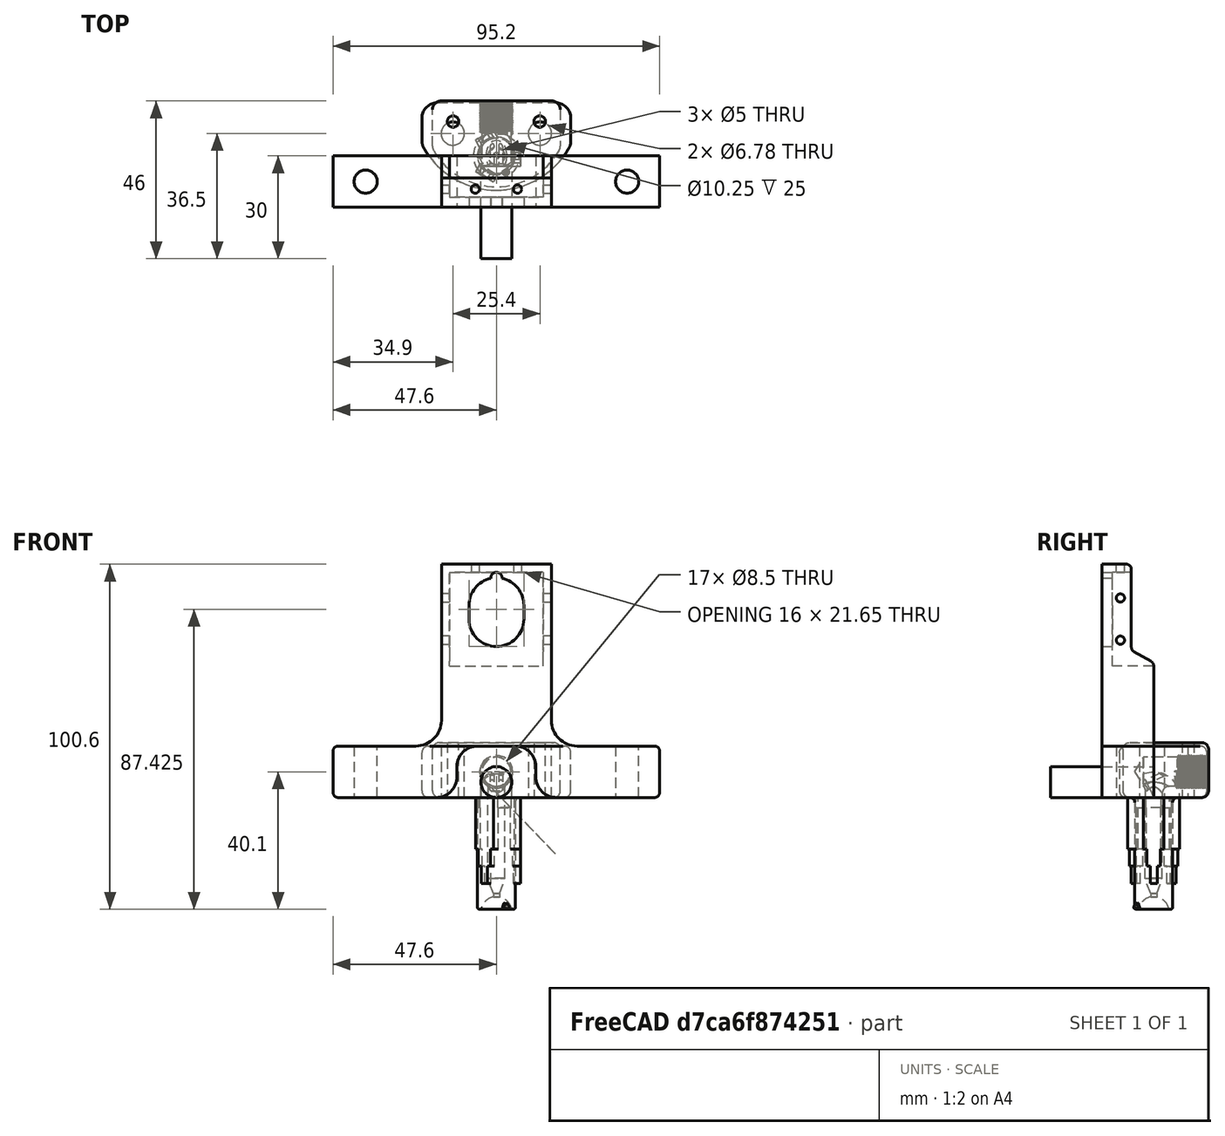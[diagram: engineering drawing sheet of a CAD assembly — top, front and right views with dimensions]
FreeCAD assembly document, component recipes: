
FREECAD ASSEMBLY — COMPONENT RECIPES ("Integrated-Inexpensive-Treadmill")

This assembly document has 6 components, labeled P0..P5 below (a component is one placed body or linked part). 6 of them carry a construction recipe — the FreeCAD feature program that regenerates the part from scratch, quoted from this document or its linked companion documents; the rest are supplied as boundary geometry only. No exploded tour is included for this assembly.
COMPONENT P0 — recipe-attached ("imperialBasePart", modeled in this document).
Construction recipe (the document's own serialized feature program — sketch geometry with constraints, then the solid features built on it; lengths are millimeters unless a unit is written):

FEATURE [Sketcher::SketchObject] Sketch005
  FullyConstrained = true
  MapMode = 5
  Support = -> [XY_Plane002]
  sketch-geometry (1):
    g0: Circle CenterX=0 CenterY=0 CenterZ=0 NormalX=0 NormalY=0 NormalZ=1 AngleXU=0 Radius=2.5
  constraints (2):
    c: Diameter(g0) = 5
    c: Coincident(g0,g-1)
FEATURE [Sketcher::SketchObject] Sketch007  label="imperialBaseSketch"
  FullyConstrained = true
  MapMode = 5
  Support = -> [XY_Plane002]
  sketch-geometry (16):
    g0: LineSegment StartX=-21.7 StartY=4.43042 StartZ=0 EndX=-21.7 EndY=11 EndZ=0
    g1: LineSegment StartX=-17.2 StartY=15.5 StartZ=0 EndX=17.2 EndY=15.5 EndZ=0
    g2: LineSegment StartX=21.7 StartY=11 StartZ=0 EndX=21.7 EndY=4.43042 EndZ=0
    g3: ArcOfCircle CenterX=1.7e-15 CenterY=14.3608 CenterZ=0 NormalX=0 NormalY=0 NormalZ=1 AngleXU=0 Radius=24.3608 StartAngle=3.66519 EndAngle=5.75959
    g4: ArcOfCircle CenterX=-17.2 CenterY=11 CenterZ=0 NormalX=0 NormalY=0 NormalZ=1 AngleXU=0 Radius=4.5 StartAngle=1.5708 EndAngle=3.14159
    g5: ArcOfCircle CenterX=17.2 CenterY=11 CenterZ=0 NormalX=0 NormalY=0 NormalZ=1 AngleXU=0 Radius=4.5 StartAngle=0 EndAngle=1.5708
    g6: ArcOfCircle CenterX=17.2 CenterY=4.43042 CenterZ=0 NormalX=0 NormalY=0 NormalZ=1 AngleXU=0 Radius=4.5 StartAngle=5.75959 EndAngle=6.28319
    g7: ArcOfCircle CenterX=-17.2 CenterY=4.43042 CenterZ=0 NormalX=0 NormalY=0 NormalZ=1 AngleXU=0 Radius=4.5 StartAngle=3.14159 EndAngle=3.66519
    g8: Circle CenterX=-12.7 CenterY=6.5 CenterZ=0 NormalX=0 NormalY=0 NormalZ=1 AngleXU=0 Radius=3.38865
    g9: Circle CenterX=12.7 CenterY=6.5 CenterZ=0 NormalX=0 NormalY=0 NormalZ=1 AngleXU=0 Radius=3.38865
    g10: GeomPoint X=-16.0886 Y=6.5 Z=0
    g11: GeomPoint X=16.0887 Y=6.5 Z=0
    g12: LineSegment StartX=-12.7 StartY=6.5 StartZ=0 EndX=12.7 EndY=6.5 EndZ=0
    g13: GeomPoint X=0 Y=-10 Z=0
    g14: GeomPoint X=0 Y=15.5 Z=0
    g15: GeomPoint X=0 Y=0 Z=0
  constraints (35):
    c: Vertical(g0)
    c: Vertical(g2)
    c: Tangent(g1,g4) = 1.5708
    c: Tangent(g0,g4) = 1.5708
    c: Tangent(g1,g5) = 1.5708
    c: Tangent(g2,g5) = 1.5708
    c: Tangent(g3,g6) = -1.5708
    c: Tangent(g2,g6) = 1.5708
    c: Tangent(g3,g7) = -1.5708
    c: Tangent(g0,g7) = 1.5708
    c: Diameter(g4) = 9
    c: Equal(g4,g7)
    c: Equal(g7,g5)
    c: Symmetric(g9,g8,g-2)
    c: Equal(g8,g9)
    c: Diameter(g9) = 6.7773
    c: PointOnObject(g10,g8)
    c: PointOnObject(g11,g9)
    c: Coincident(g12,g8)
    c: Coincident(g12,g9)
    c: PointOnObject(g11,g12)
    c: PointOnObject(g10,g12)
    c: DistanceX(g0,g8) = 9
    c: DistanceY(g8,g1) = 9
    c: Symmetric(g1,g1,g-2)
    c: PointOnObject(g13,g3)
    c: PointOnObject(g13,g-2)
    c: PointOnObject(g14,g1)
    c: PointOnObject(g14,g-2)
    c: Symmetric(g3,g3,g-2)
    c: Angle(g3) = 2.0944
    c: Coincident(g15,g-1)
    c: DistanceY(g15,g14) = 15.5
    c: DistanceY(g13,g15) = 10
    c: DistanceX(g8,g9) = 25.4
FEATURE [PartDesign::Pad] Pad001  label="imperialBase"
  AlongSketchNormal = false
  Direction = (0,0,1)
  Length = 15
  Length2 = 10
  Profile = -> Sketch007
  ReferenceAxis = -> Sketch007 [N_Axis]
  Type = 0
FEATURE [Sketcher::SketchObject] Sketch006
  FullyConstrained = true
  MapMode = 5
  Placement = pos=(0,15.5,0) rot=(0,0.707107,0.707107;3.14159rad)
  Support = -> [Pad001]
  sketch-geometry (1):
    g0: Circle CenterX=0 CenterY=7.5 CenterZ=0 NormalX=0 NormalY=0 NormalZ=1 AngleXU=0 Radius=4.7625
  constraints (3):
    c: PointOnObject(g0,g-2)
    c: DistanceY(g0,g-1) = -7.5
    c: Diameter(g0) = 9.525
FEATURE [PartDesign::Hole] Hole001  label="imperialThread"
  BaseFeature = -> Pad001
  CustomThreadClearance = 0
  Depth = 21
  DepthType = 0
  Diameter = 8.5
  DrillForDepth = true
  DrillPoint = 1
  DrillPointAngle = 118
  HoleCutCountersinkAngle = 90
  HoleCutCustomValues = false
  HoleCutDepth = 0
  HoleCutDiameter = 8.6
  HoleCutType = 0
  ModelThread = true
  Profile = -> Sketch006
  Tapered = false
  TaperedAngle = 90
  ThreadClass = 0
  ThreadDepth = 9
  ThreadDepthType = 1
  ThreadDirection = 0
  ThreadFit = 0
  ThreadSize = 12
  ThreadType = 4
  Threaded = true
  UseCustomThreadClearance = false
FEATURE [PartDesign::Pocket] Pocket001  label="imperialPocket"
  BaseFeature = -> Hole001
  Direction = (0,0,-1)
  Length = 6
  Length2 = 5
  Profile = -> Sketch005
  ReferenceAxis = -> Sketch005 [N_Axis]
  Reversed = true
  Type = 0
FEATURE [PartDesign::Fillet] Fillet004  label="outerEdgeFillet"
  Base = -> Pocket001 [Edge12,Edge14,Edge15,Edge11,Edge13,Edge6,Edge3,Edge9,Edge19,Edge10,Edge4,Edge7,Edge23,Edge22,Edge21,Edge20]
  BaseFeature = -> Pocket001
  Radius = 2
  SupportTransform = false
  UseAllEdges = false
FEATURE [PartDesign::Fillet] Fillet006
  Base = -> Fillet004 [Edge62]
  BaseFeature = -> Fillet004
  Radius = 2
  SupportTransform = false
  UseAllEdges = false
FEATURE [PartDesign::Body] Body002  label="imperialBaseBody"
  Group = -> [Sketch007,Pad001,Sketch006,Hole001,Sketch005,Pocket001,Fillet004,Fillet006]
  Origin = -> Origin002
  Tip = -> Fillet006
COMPONENT P1 — recipe-attached ("metricBasePart", modeled in this document).
Construction recipe (the document's own serialized feature program — sketch geometry with constraints, then the solid features built on it; lengths are millimeters unless a unit is written):

FEATURE [Sketcher::SketchObject] Sketch001  label="metricBaseSketch"
  FullyConstrained = true
  MapMode = 5
  Support = -> [XY_Plane001]
  sketch-geometry (16):
    g0: LineSegment StartX=-18.625 StartY=2.80977 StartZ=0 EndX=-18.625 EndY=13.5 EndZ=0
    g1: LineSegment StartX=-16.125 StartY=16 StartZ=0 EndX=16.125 EndY=16 EndZ=0
    g2: LineSegment StartX=18.625 StartY=13.5 StartZ=0 EndX=18.625 EndY=2.80977 EndZ=0
    g3: ArcOfCircle CenterX=1e-15 CenterY=12.1195 CenterZ=0 NormalX=0 NormalY=0 NormalZ=1 AngleXU=0 Radius=21.1195 StartAngle=3.66519 EndAngle=5.75959
    g4: ArcOfCircle CenterX=-16.125 CenterY=13.5 CenterZ=0 NormalX=0 NormalY=0 NormalZ=1 AngleXU=0 Radius=2.5 StartAngle=1.5708 EndAngle=3.14159
    g5: ArcOfCircle CenterX=16.125 CenterY=13.5 CenterZ=0 NormalX=0 NormalY=0 NormalZ=1 AngleXU=0 Radius=2.5 StartAngle=0 EndAngle=1.5708
    g6: ArcOfCircle CenterX=16.125 CenterY=2.80977 CenterZ=0 NormalX=0 NormalY=0 NormalZ=1 AngleXU=0 Radius=2.5 StartAngle=5.75959 EndAngle=6.28319
    g7: ArcOfCircle CenterX=-16.125 CenterY=2.80977 CenterZ=0 NormalX=0 NormalY=0 NormalZ=1 AngleXU=0 Radius=2.5 StartAngle=3.14159 EndAngle=3.66519
    g8: Circle CenterX=-12.625 CenterY=10 CenterZ=0 NormalX=0 NormalY=0 NormalZ=1 AngleXU=0 Radius=1.675
    g9: Circle CenterX=12.625 CenterY=10 CenterZ=0 NormalX=0 NormalY=0 NormalZ=1 AngleXU=0 Radius=1.675
    g10: GeomPoint X=-14.3 Y=10 Z=0
    g11: GeomPoint X=14.3 Y=10 Z=0
    g12: LineSegment StartX=-12.625 StartY=10 StartZ=0 EndX=12.625 EndY=10 EndZ=0
    g13: GeomPoint X=0 Y=-9 Z=0
    g14: GeomPoint X=0 Y=16 Z=0
    g15: GeomPoint X=0 Y=10 Z=0
  constraints (36):
    c: Vertical(g0)
    c: Vertical(g2)
    c: Tangent(g1,g4) = 1.5708
    c: Tangent(g0,g4) = 1.5708
    c: Tangent(g1,g5) = 1.5708
    c: Tangent(g2,g5) = 1.5708
    c: Tangent(g3,g6) = -1.5708
    c: Tangent(g2,g6) = 1.5708
    c: Tangent(g3,g7) = -1.5708
    c: Tangent(g0,g7) = 1.5708
    c: Diameter(g4) = 5
    c: Equal(g4,g7)
    c: Equal(g7,g5)
    c: Symmetric(g9,g8,g-2)
    c: Equal(g8,g9)
    c: Diameter(g9) = 3.35
    c: PointOnObject(g10,g8)
    c: PointOnObject(g11,g9)
    c: Coincident(g12,g8)
    c: Coincident(g12,g9)
    c: PointOnObject(g11,g12)
    c: PointOnObject(g10,g12)
    c: DistanceX(g10,g11) = 28.6
    c: DistanceX(g0,g8) = 6
    c: DistanceY(g8,g1) = 6
    c: Symmetric(g1,g1,g-2)
    c: PointOnObject(g13,g3)
    c: PointOnObject(g13,g-2)
    c: PointOnObject(g14,g1)
    c: PointOnObject(g14,g-2)
    c: Symmetric(g3,g3,g-2)
    c: Angle(g3) = 2.0944
    c: PointOnObject(g15,g12)
    c: PointOnObject(g15,g-2)
    c: DistanceY(g-1,g15) = 10
    c: DistanceY(g13,g-1) = 9
FEATURE [Sketcher::SketchObject] Sketch003
  FullyConstrained = true
  MapMode = 5
  Support = -> [XY_Plane001]
  sketch-geometry (1):
    g0: Circle CenterX=0 CenterY=0 CenterZ=0 NormalX=0 NormalY=0 NormalZ=1 AngleXU=0 Radius=2.5
  constraints (2):
    c: Diameter(g0) = 5
    c: Coincident(g0,g-1)
FEATURE [PartDesign::Pad] Pad  label="metricBase"
  Direction = (0,0,1)
  Length = 16
  Length2 = 10
  Profile = -> Sketch001
  ReferenceAxis = -> Sketch001 [N_Axis]
  Type = 0
FEATURE [Sketcher::SketchObject] Sketch002
  FullyConstrained = true
  MapMode = 5
  Placement = pos=(0,16,0) rot=(0,0.707107,0.707107;3.14159rad)
  Support = -> [Pad]
  sketch-geometry (1):
    g0: Circle CenterX=0 CenterY=7.5 CenterZ=0 NormalX=0 NormalY=0 NormalZ=1 AngleXU=0 Radius=4.7625
  constraints (3):
    c: PointOnObject(g0,g-2)
    c: DistanceY(g0,g-1) = -7.5
    c: Diameter(g0) = 9.525
FEATURE [PartDesign::Hole] Hole  label="metricThread"
  BaseFeature = -> Pad
  CustomThreadClearance = 0
  Depth = 19
  DepthType = 0
  Diameter = 8.5
  DrillForDepth = false
  DrillPoint = 0
  DrillPointAngle = 118
  HoleCutCountersinkAngle = 90
  HoleCutCustomValues = false
  HoleCutDepth = 0
  HoleCutDiameter = 8.6
  HoleCutType = 0
  ModelThread = true
  Profile = -> Sketch002
  Tapered = false
  TaperedAngle = 90
  ThreadClass = 0
  ThreadDepth = 9
  ThreadDepthType = 1
  ThreadDirection = 0
  ThreadFit = 0
  ThreadSize = 12
  ThreadType = 4
  Threaded = true
  UseCustomThreadClearance = false
FEATURE [PartDesign::Pocket] Pocket  label="metricAirOutlet"
  BaseFeature = -> Hole
  Direction = (0,0,-1)
  Length = 10
  Length2 = 5
  Profile = -> Sketch003
  ReferenceAxis = -> Sketch003 [N_Axis]
  Reversed = true
  Type = 0
FEATURE [PartDesign::Fillet] Fillet  label="BodyFillet"
  Base = -> Pocket [Edge12,Edge9,Edge3,Edge6,Edge11,Edge15,Edge13,Edge14,Edge19,Edge10,Edge4,Edge7,Edge23,Edge22,Edge21,Edge20]
  BaseFeature = -> Pocket
  Radius = 2
  SupportTransform = false
  UseAllEdges = false
FEATURE [PartDesign::Fillet] Fillet005  label="AirOutletFillet"
  Base = -> Fillet [Edge62]
  BaseFeature = -> Fillet
  Radius = 2
  SupportTransform = false
  UseAllEdges = false
FEATURE [PartDesign::Body] Body001  label="metricBaseBody"
  Group = -> [Sketch001,Pad,Sketch002,Hole,Sketch003,Pocket,Fillet,Fillet005]
  Origin = -> Origin001
  Tip = -> Fillet005
COMPONENT P2 — recipe-attached ("LightFixture", modeled in this document).
Construction recipe (the document's own serialized feature program — sketch geometry with constraints, then the solid features built on it; lengths are millimeters unless a unit is written):

FEATURE [Sketcher::SketchObject] Sketch017
  FullyConstrained = true
  MapMode = 5
  Support = -> [XY_Plane011]
  sketch-geometry (4):
    g0: LineSegment StartX=-4.5 StartY=3 StartZ=0 EndX=-4.5 EndY=0 EndZ=0
    g1: LineSegment StartX=-4.5 StartY=0 StartZ=0 EndX=4.5 EndY=0 EndZ=0
    g2: LineSegment StartX=4.5 StartY=0 StartZ=0 EndX=4.5 EndY=3 EndZ=0
    g3: ArcOfCircle CenterX=-3e-16 CenterY=3 CenterZ=0 NormalX=0 NormalY=0 NormalZ=1 AngleXU=0 Radius=4.5 StartAngle=0 EndAngle=3.14159
  constraints (12):
    c: PointOnObject(g0,g-1)
    c: Vertical(g0)
    c: Coincident(g0,g1)
    c: PointOnObject(g1,g-1)
    c: Coincident(g1,g2)
    c: Coincident(g3,g0)
    c: Coincident(g3,g2)
    c: Vertical(g2)
    c: Diameter(g3) = 9
    c: DistanceY(g0,g0) = 3
    c: Symmetric(g2,g0,g-2)
    c: Angle(g3) = 3.14159
FEATURE [PartDesign::Revolution] Revolution001  label="LightBody"
  Angle = 115
  Axis = (1,0,0)
  Base = (0,0,0)
  Profile = -> Sketch017
  ReferenceAxis = -> X_Axis011
FEATURE [Sketcher::SketchObject] Sketch018
  FullyConstrained = true
  MapMode = 5
  Placement = pos=(0,0,0) rot=(1,0,0;2.00713rad)
  Support = -> [Revolution001]
  sketch-geometry (2):
    g0: Circle CenterX=-1.27 CenterY=5 CenterZ=0 NormalX=0 NormalY=0 NormalZ=1 AngleXU=0 Radius=0.635
    g1: Circle CenterX=1.27 CenterY=5 CenterZ=0 NormalX=0 NormalY=0 NormalZ=1 AngleXU=0 Radius=0.635
  constraints (5):
    c: Symmetric(g1,g0,g-2)
    c: DistanceX(g0,g1) = 2.54
    c: Diameter(g1) = 1.27
    c: Equal(g0,g1)
    c: DistanceY(g-1,g1) = 5
FEATURE [PartDesign::Pocket] Pocket005  label="LED_Mounts"
  BaseFeature = -> Revolution001
  Direction = (0,0.906308,0.422618)
  Length = 5
  Length2 = 5
  Profile = -> Sketch018
  ReferenceAxis = -> Sketch018 [N_Axis]
  Type = 1
FEATURE [PartDesign::Body] Body005  label="Light"
  Group = -> [Sketch017,Revolution001,Sketch018,Pocket005]
  Origin = -> Origin011
  Tip = -> Pocket005
COMPONENT P3 — recipe-attached ("Connector", modeled in this document).
Construction recipe (the document's own serialized feature program — sketch geometry with constraints, then the solid features built on it; lengths are millimeters unless a unit is written):

FEATURE [Sketcher::SketchObject] Sketch019
  FullyConstrained = true
  MapMode = 5
  Placement = pos=(0,0,0) rot=(1,0,0;1.5708rad)
  Support = -> [XZ_Plane014]
  sketch-geometry (1):
    g0: Circle CenterX=0 CenterY=4.5 CenterZ=0 NormalX=0 NormalY=0 NormalZ=1 AngleXU=0 Radius=4.5
  constraints (3):
    c: PointOnObject(g0,g-2)
    c: Diameter(g0) = 9
    c: PointOnObject(g-1,g0)
FEATURE [PartDesign::Pad] Pad007  label="Rod"
  Direction = (0,-1,-2e-16)
  Length = 30
  Length2 = 10
  Placement = pos=(0,0,0) rot=(1,0,0;1.5708rad)
  Profile = -> Sketch019
  ReferenceAxis = -> Sketch019 [N_Axis]
  Type = 0
FEATURE [PartDesign::Body] Body006  label="ConnectorRod"
  Group = -> [Sketch019,Pad007]
  Origin = -> Origin013
  Tip = -> Pad007
COMPONENT P4 — recipe-attached ("FlirCameraHolder", modeled in this document).
Construction recipe (the document's own serialized feature program — sketch geometry with constraints, then the solid features built on it; lengths are millimeters unless a unit is written):

FEATURE [Sketcher::SketchObject] Sketch020
  FullyConstrained = true
  MapMode = 5
  Placement = pos=(0,0,0) rot=(1,0,0;1.5708rad)
  Support = -> [XZ_Plane016]
  expr: Constraints[20] = <<SphereHolderParameters>>.tubeheight + 20mm
  sketch-geometry (25):
    g0: LineSegment StartX=-47.6 StartY=1.5 StartZ=0 EndX=-47.6 EndY=13.5 EndZ=0
    g1: LineSegment StartX=-46.1 StartY=15 StartZ=0 EndX=-23.5 EndY=15 EndZ=0
    g2: LineSegment StartX=-16 StartY=22.5 StartZ=0 EndX=-16 EndY=68 EndZ=0
    g3: LineSegment StartX=-16 StartY=68 StartZ=0 EndX=16 EndY=68 EndZ=0
    g4: LineSegment StartX=16 StartY=68 StartZ=0 EndX=16 EndY=22.5 EndZ=0
    g5: LineSegment StartX=23.5 StartY=15 StartZ=0 EndX=46.1 EndY=15 EndZ=0
    g6: LineSegment StartX=47.6 StartY=13.5 StartZ=0 EndX=47.6 EndY=1.5 EndZ=0
    g7: LineSegment StartX=46.1 StartY=0 StartZ=0 EndX=17.5 EndY=0 EndZ=0
    g8: LineSegment StartX=-11.5 StartY=6 StartZ=0 EndX=-11.5 EndY=9 EndZ=0
    g9: LineSegment StartX=-5.5 StartY=15 StartZ=0 EndX=5.5 EndY=15 EndZ=0
    g10: LineSegment StartX=11.5 StartY=9 StartZ=0 EndX=11.5 EndY=6 EndZ=0
    g11: LineSegment StartX=-17.5 StartY=0 StartZ=0 EndX=-46.1 EndY=2e-16 EndZ=0
    g12: LineSegment StartX=-16 StartY=68 StartZ=0 EndX=16 EndY=36 EndZ=0
    g13: LineSegment StartX=16 StartY=68 StartZ=0 EndX=-16 EndY=36 EndZ=0
    g14: GeomPoint X=7e-15 Y=52 Z=0
    g15: ArcOfCircle CenterX=-17.5 CenterY=6 CenterZ=0 NormalX=0 NormalY=0 NormalZ=1 AngleXU=0 Radius=6 StartAngle=4.71239 EndAngle=6.28319
    g16: ArcOfCircle CenterX=-5.5 CenterY=9 CenterZ=0 NormalX=0 NormalY=0 NormalZ=1 AngleXU=0 Radius=6 StartAngle=1.5708 EndAngle=3.14159
    g17: ArcOfCircle CenterX=5.5 CenterY=9 CenterZ=0 NormalX=0 NormalY=0 NormalZ=1 AngleXU=0 Radius=6 StartAngle=0 EndAngle=1.5708
    g18: ArcOfCircle CenterX=17.5 CenterY=6 CenterZ=0 NormalX=0 NormalY=0 NormalZ=1 AngleXU=0 Radius=6 StartAngle=3.14159 EndAngle=4.71239
    g19: ArcOfCircle CenterX=23.5 CenterY=22.5 CenterZ=0 NormalX=0 NormalY=0 NormalZ=1 AngleXU=0 Radius=7.5 StartAngle=3.14159 EndAngle=4.71239
    g20: ArcOfCircle CenterX=-23.5 CenterY=22.5 CenterZ=0 NormalX=0 NormalY=0 NormalZ=1 AngleXU=0 Radius=7.5 StartAngle=4.71239 EndAngle=6.28319
    g21: ArcOfCircle CenterX=46.1 CenterY=13.5 CenterZ=0 NormalX=0 NormalY=0 NormalZ=1 AngleXU=0 Radius=1.5 StartAngle=3e-16 EndAngle=1.5708
    g22: ArcOfCircle CenterX=-46.1 CenterY=13.5 CenterZ=0 NormalX=0 NormalY=0 NormalZ=1 AngleXU=0 Radius=1.5 StartAngle=1.5708 EndAngle=3.14159
    g23: ArcOfCircle CenterX=46.1 CenterY=1.5 CenterZ=0 NormalX=0 NormalY=0 NormalZ=1 AngleXU=0 Radius=1.5 StartAngle=4.71239 EndAngle=6.28319
    g24: ArcOfCircle CenterX=-46.1 CenterY=1.5 CenterZ=0 NormalX=0 NormalY=0 NormalZ=1 AngleXU=0 Radius=1.5 StartAngle=3.14159 EndAngle=4.71239
  constraints (61):
    c: Vertical(g0)
    c: Horizontal(g1)
    c: Vertical(g2)
    c: Coincident(g2,g3)
    c: Horizontal(g3)
    c: Coincident(g3,g4)
    c: Vertical(g4)
    c: Horizontal(g5)
    c: Vertical(g6)
    c: Vertical(g8)
    c: Horizontal(g9)
    c: Vertical(g10)
    c: Coincident(g12,g2)
    c: PointOnObject(g12,g4)
    c: Coincident(g13,g3)
    c: PointOnObject(g13,g2)
    c: PointOnObject(g14,g13)
    c: PointOnObject(g14,g12)
    c: Angle(g13,g-2) = 0.785398
    c: Symmetric(g12,g13,g-2)
    c: DistanceY(g-1,g14) = 52
    c: Tangent(g11,g15) = 1.5708
    c: Tangent(g8,g15) = -1.5708
    c: Tangent(g8,g16) = 1.5708
    c: Tangent(g9,g16) = 1.5708
    c: Tangent(g9,g17) = 1.5708
    c: Tangent(g10,g17) = 1.5708
    c: Tangent(g10,g18) = -1.5708
    c: Tangent(g7,g18) = 1.5708
    c: Tangent(g4,g19) = -1.5708
    c: Tangent(g5,g19) = -1.5708
    c: Tangent(g2,g20) = -1.5708
    c: Tangent(g1,g20) = -1.5708
    c: Equal(g20,g19)
    c: Horizontal(g5,g1)
    c: DistanceX(g2,g3) = 32
    c: Tangent(g5,g21) = 1.5708
    c: Tangent(g6,g21) = 1.5708
    c: Tangent(g1,g22) = 1.5708
    c: Tangent(g0,g22) = 1.5708
    c: Tangent(g7,g23) = 1.5708
    c: Tangent(g6,g23) = 1.5708
    c: Tangent(g0,g24) = 1.5708
    c: Tangent(g11,g24) = 1.5708
    c: Equal(g22,g21)
    c: Equal(g21,g23)
    c: Equal(g23,g24)
    c: Diameter(g24) = 3
    c: PointOnObject(g11,g-1)
    c: Equal(g18,g17)
    c: Equal(g17,g16)
    c: Equal(g16,g15)
    c: Diameter(g15) = 12
    c: PointOnObject(g11,g-1)
    c: DistanceY(g-1,g5) = 15
    c: Symmetric(g8,g10,g-2)
    c: DistanceX(g8,g10) = 23
    c: DistanceY(g-1,g9) = 15
    c: Diameter(g20) = 15
    c: DistanceX(g0,g6) = 95.2
    c: Symmetric(g11,g7,g-2)
FEATURE [PartDesign::Pad] Pad008  label="OuterHull"
  Direction = (0,-1,2e-16)
  Length = 15
  Length2 = 10
  Placement = pos=(0,0,0) rot=(1,0,0;1.5708rad)
  Profile = -> Sketch020
  ReferenceAxis = -> Sketch020 [N_Axis]
  Type = 0
FEATURE [Sketcher::SketchObject] Sketch021
  ExternalGeometry = -> [Pad008]
  FullyConstrained = true
  MapMode = 5
  Placement = pos=(0,1e-16,0) rot=(-1,0,0;1.5708rad)
  Support = -> [Pad008]
  sketch-geometry (6):
    g0: LineSegment StartX=16 StartY=-68 StartZ=0 EndX=-52 EndY=0 EndZ=0
    g1: LineSegment StartX=-16 StartY=-68 StartZ=0 EndX=52 EndY=0 EndZ=0
    g2: LineSegment StartX=13.65 StartY=-65.65 StartZ=0 EndX=-13.65 EndY=-65.65 EndZ=0
    g3: LineSegment StartX=-13.65 StartY=-65.65 StartZ=0 EndX=-13.65 EndY=-38.35 EndZ=0
    g4: LineSegment StartX=-13.65 StartY=-38.35 StartZ=0 EndX=13.65 EndY=-38.35 EndZ=0
    g5: LineSegment StartX=13.65 StartY=-38.35 StartZ=0 EndX=13.65 EndY=-65.65 EndZ=0
  constraints (18):
    c: Coincident(g0,g-3)
    c: PointOnObject(g0,g-1)
    c: Coincident(g1,g-3)
    c: PointOnObject(g1,g-1)
    c: Angle(g1) = 0.785398
    c: Angle(g0) = 2.35619
    c: Coincident(g2,g3)
    c: Coincident(g3,g4)
    c: Coincident(g4,g5)
    c: Coincident(g5,g2)
    c: Horizontal(g2)
    c: Horizontal(g4)
    c: Vertical(g3)
    c: Vertical(g5)
    c: PointOnObject(g2,g0)
    c: PointOnObject(g3,g0)
    c: DistanceX(g3,g2) = 27.3
    c: PointOnObject(g2,g1)
FEATURE [PartDesign::Pocket] Pocket006  label="CameraCutout"
  BaseFeature = -> Pad008
  Direction = (0,-1,2e-16)
  Length = 12
  Length2 = 5
  Placement = pos=(0,0,0) rot=(1,0,0;1.5708rad)
  Profile = -> Sketch021
  ReferenceAxis = -> Sketch021 [N_Axis]
  Type = 0
FEATURE [Sketcher::SketchObject] Sketch022
  ExternalGeometry = -> [Pocket006]
  FullyConstrained = true
  MapMode = 5
  Placement = pos=(0,-12,2.6e-15) rot=(-1,0,0;1.5708rad)
  Support = -> [Pocket006]
  sketch-geometry (12):
    g0: LineSegment StartX=13.65 StartY=-65.65 StartZ=0 EndX=-52 EndY=0 EndZ=0
    g1: LineSegment StartX=-13.65 StartY=-65.65 StartZ=0 EndX=52 EndY=0 EndZ=0
    g2: GeomPoint X=0 Y=-52 Z=0
    g3: ArcOfCircle CenterX=0 CenterY=-56 CenterZ=0 NormalX=0 NormalY=0 NormalZ=1 AngleXU=0 Radius=8 StartAngle=3.14159 EndAngle=4.50577
    g4: ArcOfCircle CenterX=0 CenterY=-52 CenterZ=0 NormalX=0 NormalY=0 NormalZ=1 AngleXU=0 Radius=8 StartAngle=0 EndAngle=3.14159
    g5: LineSegment StartX=8 StartY=-56 StartZ=0 EndX=8 EndY=-52 EndZ=0
    g6: LineSegment StartX=-8 StartY=-52 StartZ=0 EndX=-8 EndY=-56 EndZ=0
    g7: GeomPoint X=0 Y=-64 Z=0
    g8: GeomPoint X=0 Y=-44 Z=0
    g9: ArcOfCircle CenterX=0 CenterY=-64 CenterZ=0 NormalX=0 NormalY=0 NormalZ=1 AngleXU=0 Radius=1.65 StartAngle=3.03828 EndAngle=6.38649
    g10: GeomPoint X=0 Y=-65.65 Z=0
    g11: ArcOfCircle CenterX=0 CenterY=-56 CenterZ=0 NormalX=0 NormalY=0 NormalZ=1 AngleXU=0 Radius=8 StartAngle=4.91901 EndAngle=6.28318
  constraints (30):
    c: Coincident(g0,g-3)
    c: PointOnObject(g0,g-1)
    c: Coincident(g1,g-3)
    c: PointOnObject(g1,g-1)
    c: Angle(g0) = 2.35619
    c: Angle(g1) = 0.785398
    c: PointOnObject(g2,g1)
    c: PointOnObject(g2,g-2)
    c: Coincident(g11,g5) = -1.5708
    c: Tangent(g5,g4) = -1.5708
    c: Tangent(g4,g6) = -1.5708
    c: Tangent(g6,g3) = -1.5708
    c: Equal(g3,g4)
    c: PointOnObject(g3,g-2)
    c: DistanceX(g4,g4) = 16
    c: PointOnObject(g7,g-2)
    c: PointOnObject(g8,g4)
    c: PointOnObject(g8,g-2)
    c: PointOnObject(g7,g3)
    c: DistanceY(g7,g8) = 20
    c: Coincident(g4,g2)
    c: Coincident(g9,g7)
    c: PointOnObject(g10,g9)
    c: PointOnObject(g10,g-2)
    c: PointOnObject(g10,g-3)
    c: Equal(g3,g11)
    c: Coincident(g3,g9)
    c: Coincident(g11,g9)
    c: Coincident(g3,g11)
    c: Vertical(g5)
FEATURE [PartDesign::Pocket] Pocket007  label="LensWindow"
  BaseFeature = -> Pocket006
  Direction = (0,-1,2e-16)
  Length = 5
  Length2 = 5
  Placement = pos=(0,0,0) rot=(1,0,0;1.5708rad)
  Profile = -> Sketch022
  ReferenceAxis = -> Sketch022 [N_Axis]
  Type = 0
FEATURE [Sketcher::SketchObject] Sketch023
  FullyConstrained = true
  MapMode = 5
  Placement = pos=(0,0,0) rot=(1,0,0;3.14159rad)
  Support = -> [Pocket007]
  sketch-geometry (2):
    g0: Circle CenterX=38.1 CenterY=7.5 CenterZ=0 NormalX=0 NormalY=0 NormalZ=1 AngleXU=0 Radius=3.3665
    g1: Circle CenterX=-38.1 CenterY=7.5 CenterZ=0 NormalX=0 NormalY=0 NormalZ=1 AngleXU=0 Radius=3.3665
  constraints (5):
    c: Equal(g1,g0)
    c: Diameter(g0) = 6.733
    c: DistanceY(g-1,g1) = 7.5
    c: Symmetric(g1,g0,g-2)
    c: DistanceX(g1,g0) = 76.2
FEATURE [PartDesign::Pocket] Pocket008  label="BottomScrews"
  BaseFeature = -> Pocket007
  Direction = (0,7e-16,1)
  Length = 5
  Length2 = 5
  Placement = pos=(0,0,0) rot=(1,0,0;1.5708rad)
  Profile = -> Sketch023
  ReferenceAxis = -> Sketch023 [N_Axis]
  Type = 1
FEATURE [Sketcher::SketchObject] Sketch024
  FullyConstrained = true
  MapMode = 5
  Placement = pos=(0,2.99e-14,68) rot=(0,0,1;3.14159rad)
  Support = -> [Pocket008]
  sketch-geometry (2):
    g0: Circle CenterX=-6.15 CenterY=9.7 CenterZ=0 NormalX=0 NormalY=0 NormalZ=1 AngleXU=0 Radius=1.2
    g1: Circle CenterX=6.15 CenterY=9.7 CenterZ=0 NormalX=0 NormalY=0 NormalZ=1 AngleXU=0 Radius=1.2
  constraints (5):
    c: Symmetric(g0,g1,g-2)
    c: Equal(g1,g0)
    c: Diameter(g0) = 2.4
    c: DistanceY(g-1,g0) = 9.7
    c: DistanceX(g0,g1) = 12.3
FEATURE [PartDesign::Pocket] Pocket009  label="TopScrews"
  BaseFeature = -> Pocket008
  Direction = (0,-8e-16,-1)
  Length = 5
  Length2 = 5
  Placement = pos=(0,0,0) rot=(1,0,0;1.5708rad)
  Profile = -> Sketch024
  ReferenceAxis = -> Sketch024 [N_Axis]
  Type = 2
FEATURE [Sketcher::SketchObject] Sketch026
  ExternalGeometry = -> [Pocket009]
  FullyConstrained = true
  MapMode = 5
  Placement = pos=(-13.65,0,0) rot=(0.707107,0,0.707107;3.14159rad)
  Support = -> [Pocket009]
  sketch-geometry (3):
    g0: Circle CenterX=45.85 CenterY=9.7 CenterZ=0 NormalX=0 NormalY=0 NormalZ=1 AngleXU=0 Radius=1.2
    g1: Circle CenterX=58.15 CenterY=9.7 CenterZ=0 NormalX=0 NormalY=0 NormalZ=1 AngleXU=0 Radius=1.2
    g2: LineSegment StartX=52 StartY=12 StartZ=0 EndX=52 EndY=0 EndZ=0
  constraints (8):
    c: PointOnObject(g2,g-5)
    c: PointOnObject(g2,g-1)
    c: Symmetric(g-5,g-5,g2)
    c: Symmetric(g1,g0,g2)
    c: DistanceX(g0,g1) = 12.3
    c: DistanceY(g1,g2) = 2.3
    c: Equal(g1,g0)
    c: Diameter(g0) = 2.4
FEATURE [PartDesign::Pocket] Pocket010  label="SideScrews"
  BaseFeature = -> Pocket009
  Direction = (-1,0,2e-16)
  Length = 5
  Length2 = 5
  Midplane = true
  Placement = pos=(0,0,0) rot=(1,0,0;1.5708rad)
  Profile = -> Sketch026
  ReferenceAxis = -> Sketch026 [N_Axis]
  Type = 1
FEATURE [Sketcher::SketchObject] Sketch027
  ExternalGeometry = -> [Pocket010]
  FullyConstrained = true
  MapMode = 5
  Placement = pos=(16,0,0) rot=(0.707107,0,0.707107;3.14159rad)
  Support = -> [Pocket010]
  sketch-geometry (7):
    g0: ArcOfCircle CenterX=66.5 CenterY=8 CenterZ=0 NormalX=0 NormalY=0 NormalZ=1 AngleXU=0 Radius=1.5 StartAngle=4.71239 EndAngle=6.28319
    g1: ArcOfCircle CenterX=38.35 CenterY=1.5 CenterZ=0 NormalX=0 NormalY=0 NormalZ=1 AngleXU=0 Radius=1.5 StartAngle=4.71239 EndAngle=5.75959
    g2: LineSegment StartX=43.8348 StartY=6.5 StartZ=0 EndX=66.5 EndY=6.5 EndZ=0
    g3: ArcOfCircle CenterX=43.8348 CenterY=5 CenterZ=0 NormalX=0 NormalY=0 NormalZ=1 AngleXU=0 Radius=1.5 StartAngle=1.5708 EndAngle=2.61799
    g4: LineSegment StartX=42.5358 StartY=5.75 StartZ=0 EndX=39.649 EndY=0.75 EndZ=0
    g5: LineSegment StartX=68 StartY=8 StartZ=0 EndX=68 EndY=0 EndZ=0
    g6: LineSegment StartX=68 StartY=0 StartZ=0 EndX=38.35 EndY=-8.4e-15 EndZ=0
  constraints (17):
    c: Coincident(g1,g-4)
    c: Perpendicular(g1,g-4)
    c: Diameter(g1) = 3
    c: Diameter(g0) = 3
    c: Tangent(g0,g-3) = -1.5708
    c: Horizontal(g2)
    c: Tangent(g4,g3) = -1.5708
    c: Diameter(g3) = 3
    c: Tangent(g3,g2) = 1.5708
    c: Tangent(g4,g1) = 1.5708
    c: Angle(g4) = -2.0944
    c: DistanceY(g-3,g0) = 6.5
    c: Tangent(g2,g0) = -1.5708
    c: Coincident(g5,g0)
    c: Coincident(g5,g-3)
    c: Coincident(g6,g5)
    c: Coincident(g6,g1)
FEATURE [PartDesign::Pocket] Pocket011  label="RaceLine"
  BaseFeature = -> Pocket010
  Direction = (-1,0,2e-16)
  Length = 5
  Length2 = 5
  Placement = pos=(0,0,0) rot=(1,0,0;1.5708rad)
  Profile = -> Sketch027
  ReferenceAxis = -> Sketch027 [N_Axis]
  Type = 1
FEATURE [PartDesign::Body] Body007  label="CameraBody"
  Group = -> [Sketch020,Pad008,Sketch021,Pocket006,Sketch022,Pocket007,Sketch023,Pocket008,Sketch024,Pocket009,Sketch026,Pocket010,Sketch027,Pocket011]
  Origin = -> Origin015
  Tip = -> Pocket011
COMPONENT P5 — recipe-attached ("TubePart", modeled in this document).
Construction recipe (the document's own serialized feature program — sketch geometry with constraints, then the solid features built on it; lengths are millimeters unless a unit is written):

FEATURE [Sketcher::SketchObject] Sketch  label="Revolution tube cross section"
  AttachmentOffset = pos=(0,0,0) rot=(1,0,0;3.14159rad)
  FullyConstrained = true
  MapMode = 5
  Placement = pos=(0,0,0) rot=(1,0,0;4.71239rad)
  Support = -> [XZ_Plane]
  expr: Constraints[12] = <<SphereHolderParameters>>.tubeheight
  sketch-geometry (10):
    g0: LineSegment StartX=-0.9 StartY=27.9713 StartZ=0 EndX=-0.9 EndY=28.9713 EndZ=0
    g1: LineSegment StartX=-2.5 StartY=8.9584e-12 StartZ=0 EndX=-6.73953 EndY=8.9584e-12 EndZ=0
    g2: LineSegment StartX=-5.5 StartY=1.47721 StartZ=0 EndX=-5.5 EndY=32 EndZ=0
    g3: ArcOfCircle CenterX=0 CenterY=33.3803 CenterZ=0 NormalX=0 NormalY=0 NormalZ=1 AngleXU=0 Radius=4.5 StartAngle=3.41593 EndAngle=4.51103
    g4: ArcOfCircle CenterX=0 CenterY=33.3803 CenterZ=0 NormalX=0 NormalY=0 NormalZ=1 AngleXU=0 Radius=4.5 StartAngle=3.41593 EndAngle=4.71239
    g5: ArcOfCircle CenterX=-4.90473 CenterY=32 CenterZ=0 NormalX=0 NormalY=0 NormalZ=1 AngleXU=0 Radius=0.595267 StartAngle=0.274335 EndAngle=3.14159
    g6: GeomPoint X=-5.5 Y=0 Z=0
    g7: ArcOfCircle CenterX=-7 CenterY=1.47721 CenterZ=0 NormalX=0 NormalY=0 NormalZ=1 AngleXU=0 Radius=1.5 StartAngle=4.88692 EndAngle=6.28319
    g8: LineSegment StartX=-0.9 StartY=27.9713 StartZ=0 EndX=-2.5 EndY=23.5753 EndZ=0
    g9: LineSegment StartX=-2.5 StartY=23.5753 StartZ=0 EndX=-2.5 EndY=8.9599e-12 EndZ=0
  constraints (29):
    c: Vertical(g0)
    c: PointOnObject(g6,g-1)
    c: Vertical(g2)
    c: PointOnObject(g3,g-2)
    c: Coincident(g3,g0)
    c: DistanceX(g6,g-1) = 5.5
    c: Coincident(g4,g3)
    c: PointOnObject(g4,g-2)
    c: Coincident(g3,g4)
    c: Tangent(g5,g3) = 1.5708
    c: Tangent(g5,g2) = 1.5708
    c: DistanceY(g0,g3) = 3.19
    c: DistanceY(g-1,g2) = 32
    c: PointOnObject(g6,g2)
    c: PointOnObject(g6,g1)
    c: Coincident(g7,g1)
    c: Tangent(g7,g2) = -1.5708
    c: Angle(g7) = 1.39626
    c: Diameter(g7) = 3
    c: Diameter(g3) = 9
    c: Coincident(g9,g8)
    c: Vertical(g9)
    c: Coincident(g0,g8)
    c: Coincident(g1,g9)
    c: DistanceX(g-2,g0) = -0.9
    c: Angle(g8) = 4.36332
    c: DistanceY(g0,g0) = 1
    c: Horizontal(g1)
    c: DistanceX(g1,g-1) = 2.5
FEATURE [PartDesign::Revolution] Revolution  label="Tube"
  Angle = 360
  Axis = (0,2e-16,-1)
  Base = (0,0,0)
  Placement = pos=(0,0,0) rot=(1,0,0;1.5708rad)
  Profile = -> Sketch
  ReferenceAxis = -> Sketch [V_Axis]
FEATURE [PartDesign::Plane] DatumPlane  label="Rotate120"
  AttachmentOffset = pos=(0,0,0) rot=(0,1,0;2.0944rad)
  Length = 79.989
  MapMode = 5
  Placement = pos=(0,0,0) rot=(-0.186157,0.694747,0.694747;3.50969rad)
  ResizeMode = 0
  Support = -> [YZ_Plane007]
  Width = 61.6877
FEATURE [PartDesign::Plane] DatumPlane001  label="Rotate240"
  AttachmentOffset = pos=(0,0,0) rot=(0,1,0;4.18879rad)
  Length = 79.989
  MapMode = 5
  Placement = pos=(0,0,0) rot=(-0.935113,0.250563,0.250563;4.64535rad)
  ResizeMode = 0
  Support = -> [YZ_Plane007]
  Width = 61.6877
FEATURE [Sketcher::SketchObject] Sketch008
  FullyConstrained = true
  MapMode = 5
  Placement = pos=(0,0,0) rot=(-0.186157,0.694747,0.694747;3.50969rad)
  Support = -> [DatumPlane]
  expr: Constraints[16] = Spreadsheet.tubeheight - 7mm
  expr: Constraints[17] = <<SphereHolderParameters>>.first_step
  expr: Constraints[32] = <<SphereHolderParameters>>.second_step
  sketch-geometry (12):
    g0: LineSegment StartX=-3 StartY=0 StartZ=0 EndX=3 EndY=-2e-16 EndZ=0
    g1: LineSegment StartX=2 StartY=-15 StartZ=0 EndX=2 EndY=-20 EndZ=0
    g2: LineSegment StartX=2 StartY=-20 StartZ=0 EndX=1 EndY=-20 EndZ=0
    g3: LineSegment StartX=1 StartY=-20 StartZ=0 EndX=1 EndY=-25 EndZ=0
    g4: LineSegment StartX=1 StartY=-25 StartZ=0 EndX=-1 EndY=-25 EndZ=0
    g5: LineSegment StartX=-1 StartY=-25 StartZ=0 EndX=-1 EndY=-20 EndZ=0
    g6: LineSegment StartX=-1 StartY=-20 StartZ=0 EndX=-2 EndY=-20 EndZ=0
    g7: LineSegment StartX=-2 StartY=-20 StartZ=0 EndX=-2 EndY=-15 EndZ=0
    g8: LineSegment StartX=-2 StartY=-15 StartZ=0 EndX=-3 EndY=-15 EndZ=0
    g9: LineSegment StartX=-3 StartY=-15 StartZ=0 EndX=-3 EndY=0 EndZ=0
    g10: LineSegment StartX=2 StartY=-15 StartZ=0 EndX=3 EndY=-15 EndZ=0
    g11: LineSegment StartX=3 StartY=-15 StartZ=0 EndX=3 EndY=0 EndZ=0
  constraints (33):
    c: PointOnObject(g0,g-1)
    c: Vertical(g1)
    c: Coincident(g1,g2)
    c: Horizontal(g2)
    c: Coincident(g2,g3)
    c: Vertical(g3)
    c: Coincident(g3,g4)
    c: Horizontal(g4)
    c: Coincident(g4,g5)
    c: Vertical(g5)
    c: Coincident(g5,g6)
    c: Horizontal(g6)
    c: Coincident(g6,g7)
    c: Vertical(g7)
    c: Symmetric(g0,g0,g-2)
    c: Symmetric(g5,g2,g-2)
    c: DistanceY(g3,g0) = 25
    c: DistanceY(g3,g2) = 5
    c: DistanceX(g4,g3) = 2
    c: DistanceX(g6,g1) = 4
    c: Horizontal(g8)
    c: Coincident(g9,g8)
    c: Vertical(g9)
    c: Coincident(g7,g8)
    c: Coincident(g0,g9)
    c: Horizontal(g10)
    c: Coincident(g11,g10)
    c: Vertical(g11)
    c: Coincident(g1,g10)
    c: Symmetric(g1,g7,g-2)
    c: Coincident(g0,g11)
    c: DistanceX(g8,g10) = 6
    c: DistanceY(g3,g10) = 10
FEATURE [PartDesign::Pad] Pad002
  Direction = (-0.5,0.866025,-5e-16)
  Length = 7
  Length2 = 10
  Placement = pos=(0,0,0) rot=(-0.186157,0.694747,0.694747;3.50969rad)
  Profile = -> Sketch008
  ReferenceAxis = -> Sketch008 [N_Axis]
  Type = 0
FEATURE [Sketcher::SketchObject] Sketch009
  FullyConstrained = true
  MapMode = 5
  Placement = pos=(0,0,0) rot=(0.935113,-0.250563,-0.250563;1.63783rad)
  Support = -> [DatumPlane001]
  expr: Constraints[27] = <<SphereHolderParameters>>.tubeheight - 7mm
  expr: Constraints[28] = <<SphereHolderParameters>>.first_step
  expr: Constraints[29] = <<SphereHolderParameters>>.second_step
  sketch-geometry (12):
    g0: LineSegment StartX=-3 StartY=0 StartZ=0 EndX=3 EndY=2e-16 EndZ=0
    g1: LineSegment StartX=3 StartY=2e-16 StartZ=0 EndX=3 EndY=-15 EndZ=0
    g2: LineSegment StartX=3 StartY=-15 StartZ=0 EndX=2 EndY=-15 EndZ=0
    g3: LineSegment StartX=2 StartY=-15 StartZ=0 EndX=2 EndY=-20 EndZ=0
    g4: LineSegment StartX=2 StartY=-20 StartZ=0 EndX=1 EndY=-20 EndZ=0
    g5: LineSegment StartX=1 StartY=-20 StartZ=0 EndX=1 EndY=-25 EndZ=0
    g6: LineSegment StartX=1 StartY=-25 StartZ=0 EndX=-1 EndY=-25 EndZ=0
    g7: LineSegment StartX=-1 StartY=-25 StartZ=0 EndX=-1 EndY=-20 EndZ=0
    g8: LineSegment StartX=-1 StartY=-20 StartZ=0 EndX=-2 EndY=-20 EndZ=0
    g9: LineSegment StartX=-2 StartY=-20 StartZ=0 EndX=-2 EndY=-15 EndZ=0
    g10: LineSegment StartX=-2 StartY=-15 StartZ=0 EndX=-3 EndY=-15 EndZ=0
    g11: LineSegment StartX=-3 StartY=-15 StartZ=0 EndX=-3 EndY=0 EndZ=0
  constraints (33):
    c: PointOnObject(g0,g-1)
    c: Coincident(g0,g1)
    c: Vertical(g1)
    c: Coincident(g1,g2)
    c: Horizontal(g2)
    c: Coincident(g2,g3)
    c: Vertical(g3)
    c: Coincident(g3,g4)
    c: Horizontal(g4)
    c: Coincident(g4,g5)
    c: Vertical(g5)
    c: Coincident(g5,g6)
    c: Horizontal(g6)
    c: Coincident(g6,g7)
    c: Vertical(g7)
    c: Coincident(g7,g8)
    c: Horizontal(g8)
    c: Coincident(g8,g9)
    c: Vertical(g9)
    c: Coincident(g9,g10)
    c: Horizontal(g10)
    c: Coincident(g10,g11)
    c: Coincident(g11,g0)
    c: Vertical(g11)
    c: Symmetric(g0,g0,g-2)
    c: Symmetric(g9,g2,g-2)
    c: Symmetric(g7,g4,g-2)
    c: DistanceY(g5,g0) = 25
    c: DistanceY(g6,g7) = 5
    c: DistanceY(g6,g9) = 10
    c: DistanceX(g0,g0) = 6
    c: DistanceX(g8,g3) = 4
    c: DistanceX(g6,g5) = 2
FEATURE [PartDesign::Pad] Pad003
  BaseFeature = -> Pad002
  Direction = (-0.5,-0.866025,3e-16)
  Length = 7
  Length2 = 10
  Placement = pos=(0,0,0) rot=(-0.186157,0.694747,0.694747;3.50969rad)
  Profile = -> Sketch009
  ReferenceAxis = -> Sketch009 [N_Axis]
  Type = 0
FEATURE [Sketcher::SketchObject] Sketch010
  FullyConstrained = true
  MapMode = 5
  Placement = pos=(0,0,0) rot=(0.57735,0.57735,0.57735;2.0944rad)
  Support = -> [YZ_Plane007]
  expr: Constraints[29] = <<SphereHolderParameters>>.tubeheight - 7mm
  expr: Constraints[30] = <<SphereHolderParameters>>.first_step
  expr: Constraints[31] = <<SphereHolderParameters>>.second_step
  sketch-geometry (12):
    g0: LineSegment StartX=-3 StartY=0 StartZ=0 EndX=3 EndY=0 EndZ=0
    g1: LineSegment StartX=3 StartY=0 StartZ=0 EndX=3 EndY=-15 EndZ=0
    g2: LineSegment StartX=3 StartY=-15 StartZ=0 EndX=2 EndY=-15 EndZ=0
    g3: LineSegment StartX=2 StartY=-15 StartZ=0 EndX=2 EndY=-20 EndZ=0
    g4: LineSegment StartX=2 StartY=-20 StartZ=0 EndX=1 EndY=-20 EndZ=0
    g5: LineSegment StartX=1 StartY=-20 StartZ=0 EndX=1 EndY=-25 EndZ=0
    g6: LineSegment StartX=1 StartY=-25 StartZ=0 EndX=-1 EndY=-25 EndZ=0
    g7: LineSegment StartX=-1 StartY=-25 StartZ=0 EndX=-1 EndY=-20 EndZ=0
    g8: LineSegment StartX=-1 StartY=-20 StartZ=0 EndX=-2 EndY=-20 EndZ=0
    g9: LineSegment StartX=-2 StartY=-20 StartZ=0 EndX=-2 EndY=-15 EndZ=0
    g10: LineSegment StartX=-2 StartY=-15 StartZ=0 EndX=-3 EndY=-15 EndZ=0
    g11: LineSegment StartX=-3 StartY=-15 StartZ=0 EndX=-3 EndY=0 EndZ=0
  constraints (32):
    c: PointOnObject(g0,g-1)
    c: PointOnObject(g0,g-1)
    c: Coincident(g0,g1)
    c: Vertical(g1)
    c: Coincident(g1,g2)
    c: Horizontal(g2)
    c: Coincident(g2,g3)
    c: Vertical(g3)
    c: Coincident(g3,g4)
    c: Horizontal(g4)
    c: Coincident(g4,g5)
    c: Vertical(g5)
    c: Coincident(g5,g6)
    c: Coincident(g6,g7)
    c: Coincident(g7,g8)
    c: Horizontal(g8)
    c: Coincident(g8,g9)
    c: Coincident(g9,g10)
    c: Coincident(g10,g11)
    c: Coincident(g11,g0)
    c: Vertical(g11)
    c: Vertical(g9)
    c: Symmetric(g6,g5,g-2)
    c: Symmetric(g4,g7,g-2)
    c: Symmetric(g2,g9,g-2)
    c: Symmetric(g1,g10,g-2)
    c: DistanceX(g6,g5) = 2
    c: DistanceX(g8,g3) = 4
    c: DistanceX(g10,g1) = 6
    c: DistanceY(g5,g0) = 25
    c: DistanceY(g5,g4) = 5
    c: DistanceY(g5,g2) = 10
FEATURE [PartDesign::Pad] Pad004
  BaseFeature = -> Pad003
  Direction = (1,-2e-16,3e-16)
  Length = 7
  Length2 = 10
  Placement = pos=(0,0,0) rot=(-0.186157,0.694747,0.694747;3.50969rad)
  Profile = -> Sketch010
  ReferenceAxis = -> Sketch010 [N_Axis]
  Type = 0
FEATURE [Sketcher::SketchObject] Sketch011
  FullyConstrained = true
  MapMode = 5
  Support = -> [XY_Plane007]
  sketch-geometry (1):
    g0: Circle CenterX=0 CenterY=0 CenterZ=0 NormalX=0 NormalY=0 NormalZ=1 AngleXU=0 Radius=5.25
  constraints (2):
    c: Coincident(g0,g-1)
    c: Diameter(g0) = 10.5
FEATURE [PartDesign::Pad] Pad005
  BaseFeature = -> Pad004
  Direction = (0,0,1)
  Length = 3
  Length2 = 10
  Placement = pos=(0,0,0) rot=(-0.186157,0.694747,0.694747;3.50969rad)
  Profile = -> Sketch011
  ReferenceAxis = -> Sketch011 [N_Axis]
  Reversed = true
  Type = 0
FEATURE [Sketcher::SketchObject] Sketch012
  FullyConstrained = true
  MapMode = 5
  Support = -> [XY_Plane007]
  sketch-geometry (1):
    g0: Circle CenterX=0 CenterY=0 CenterZ=0 NormalX=0 NormalY=0 NormalZ=1 AngleXU=0 Radius=5.125
  constraints (2):
    c: Coincident(g0,g-1)
    c: Diameter(g0) = 10.25
FEATURE [PartDesign::Pocket] Pocket002
  BaseFeature = -> Pad005
  Direction = (0,0,-1)
  Length = 5
  Length2 = 5
  Placement = pos=(0,0,0) rot=(-0.186157,0.694747,0.694747;3.50969rad)
  Profile = -> Sketch012
  ReferenceAxis = -> Sketch012 [N_Axis]
  Type = 1
FEATURE [PartDesign::Body] Body003  label="Steppers"
  Group = -> [DatumPlane,DatumPlane001,Sketch008,Pad002,Sketch009,Pad003,Sketch010,Pad004,Sketch011,Pad005,Sketch012,Pocket002]
  Origin = -> Origin007
  Tip = -> Pocket002
FEATURE [PartDesign::Plane] DatumPlane003
  Length = 60
  MapMode = 11
  Placement = pos=(0,0,-32) rot=(0.707107,0.707107,0;3.14159rad)
  ResizeMode = 0
  Support = -> [Revolution]
  Width = 60
FEATURE [Sketcher::SketchObject] Sketch030
  ExternalGeometry = -> [Revolution]
  FullyConstrained = true
  MapMode = 5
  Placement = pos=(0,0,-32) rot=(0.707107,0.707107,0;3.14159rad)
  Support = -> [DatumPlane003]
  sketch-geometry (3):
    g0: LineSegment StartX=0 StartY=0 StartZ=0 EndX=5.19615 EndY=3 EndZ=0
    g1: ArcOfCircle CenterX=4.76314 CenterY=2.75 CenterZ=0 NormalX=0 NormalY=0 NormalZ=1 AngleXU=0 Radius=1 StartAngle=5.14495 EndAngle=8.46862
    g2: ArcOfCircle CenterX=0 CenterY=0 CenterZ=0 NormalX=0 NormalY=0 NormalZ=1 AngleXU=0 Radius=5.5 StartAngle=0.341529 EndAngle=0.705668
  constraints (10):
    c: Coincident(g0,g-4)
    c: Distance(g0) = 6
    c: Angle(g0) = 0.523599
    c: PointOnObject(g1,g-3)
    c: PointOnObject(g1,g-3)
    c: Diameter(g1) = 2
    c: Coincident(g2,g0)
    c: Coincident(g2,g1)
    c: Coincident(g2,g1)
    c: PointOnObject(g1,g0)
FEATURE [PartDesign::Line] DatumLine001
  AttacherType = Attacher::AttachEngineLine
  Length = 20
  MapMode = 31
  Placement = pos=(2.70455,4.68441,-32) rot=(-0.377964,0.654654,0.654654;3.86433rad)
  ResizeMode = 0
  Support = -> [Sketch030]
FEATURE [PartDesign::Revolution] Revolution004  label="SensorHolderUnderpinning"
  Angle = 100
  Axis = (-0.866025,0.5,0)
  Base = (2.70455,4.68441,-32)
  BaseFeature = -> Revolution
  Placement = pos=(0,0,0) rot=(1,0,0;1.5708rad)
  Profile = -> Sketch030
  ReferenceAxis = -> DatumLine001
  Reversed = true
FEATURE [PartDesign::Revolution] Revolution005  label="SensorHolderAngle"
  Angle = 20
  Axis = (-0.866025,0.5,0)
  Base = (2.70455,4.68441,-32)
  BaseFeature = -> Revolution004
  Placement = pos=(0,0,0) rot=(1,0,0;1.5708rad)
  Profile = -> Sketch030
  ReferenceAxis = -> DatumLine001
FEATURE [Sketcher::SketchObject] Sketch031
  ExternalGeometry = -> [DatumLine001]
  FullyConstrained = true
  MapMode = 5
  Placement = pos=(-4.82593,-8.35875,-26.5183) rot=(0.996224,-0.013204,-0.085814;2.83738rad)
  Support = -> [Revolution005]
  sketch-geometry (2):
    g0: Circle CenterX=7.23 CenterY=-14.3119 CenterZ=0 NormalX=0 NormalY=0 NormalZ=1 AngleXU=0 Radius=0.35
    g1: Circle CenterX=8.10897 CenterY=-13.835 CenterZ=0 NormalX=0 NormalY=0 NormalZ=1 AngleXU=0 Radius=0.35
  constraints (6):
    c: PointOnObject(g0,g-3)
    c: PointOnObject(g1,g-3)
    c: Equal(g1,g0)
    c: Distance(g1,g0) = 1
    c: Diameter(g1) = 0.7
    c: DistanceX(g-1,g0) = 7.23
FEATURE [PartDesign::Pocket] Pocket013  label="SensorHolderWires"
  BaseFeature = -> Revolution005
  Direction = (0.17101,0.296198,0.939693)
  Length = 5
  Length2 = 5
  Midplane = true
  Placement = pos=(0,0,0) rot=(1,0,0;1.5708rad)
  Profile = -> Sketch031
  ReferenceAxis = -> Sketch031 [N_Axis]
  Type = 1
FEATURE [Sketcher::SketchObject] Sketch032
  ExternalGeometry = -> [Pocket013]
  FullyConstrained = true
  MapMode = 5
  Placement = pos=(-4.82593,-8.35875,-26.5183) rot=(0.996224,-0.013204,-0.085814;2.83738rad)
  Support = -> [Pocket013]
  sketch-geometry (4):
    g0: ArcOfCircle CenterX=7.68641 CenterY=-14.1677 CenterZ=0 NormalX=0 NormalY=0 NormalZ=1 AngleXU=0 Radius=1 StartAngle=3.11509 EndAngle=7.30388
    g1: LineSegment StartX=6.76773 StartY=-14.5627 StartZ=0 EndX=8.5184 EndY=-13.6129 EndZ=0
    g2: LineSegment StartX=6.68677 StartY=-14.1412 StartZ=0 EndX=8.20919 EndY=-13.3152 EndZ=0
    g3: LineSegment StartX=6.68677 StartY=-14.1412 StartZ=0 EndX=8.20919 EndY=-13.3152 EndZ=0
  constraints (10):
    c: PointOnObject(g0,g-3)
    c: Angle(g0) = 4.18879
    c: Coincident(g1,g-3)
    c: Coincident(g1,g-3)
    c: Coincident(g2,g0)
    c: Coincident(g2,g0)
    c: Coincident(g0,g-3)
    c: Parallel(g2,g1)
    c: Coincident(g3,g0)
    c: Coincident(g3,g0)
FEATURE [PartDesign::Pocket] Pocket014  label="SensorHolderPlateau"
  BaseFeature = -> Pocket013
  Direction = (0.17101,0.296198,0.939693)
  Length = 5
  Length2 = 5
  Placement = pos=(0,0,0) rot=(1,0,0;1.5708rad)
  Profile = -> Sketch032
  ReferenceAxis = -> Sketch032 [N_Axis]
  Reversed = true
  Type = 0
FEATURE [PartDesign::Body] Body  label="SphereTube"
  Group = -> [Sketch,Revolution,DatumPlane003,Sketch030,DatumLine001,Revolution004,Revolution005,Sketch031,Pocket013,Sketch032,Pocket014]
  Origin = -> Origin
  Placement = pos=(0,0,0) rot=(0,0,-1;2.0944rad)
  Tip = -> Pocket014
PROVENANCE & LICENSES
A FreeCAD (.FCStd) document from a public repository crawl; recipes are the document's own serialized feature recipes (and, for linked parts, companion documents' recipes).
License: cern-ohl.
